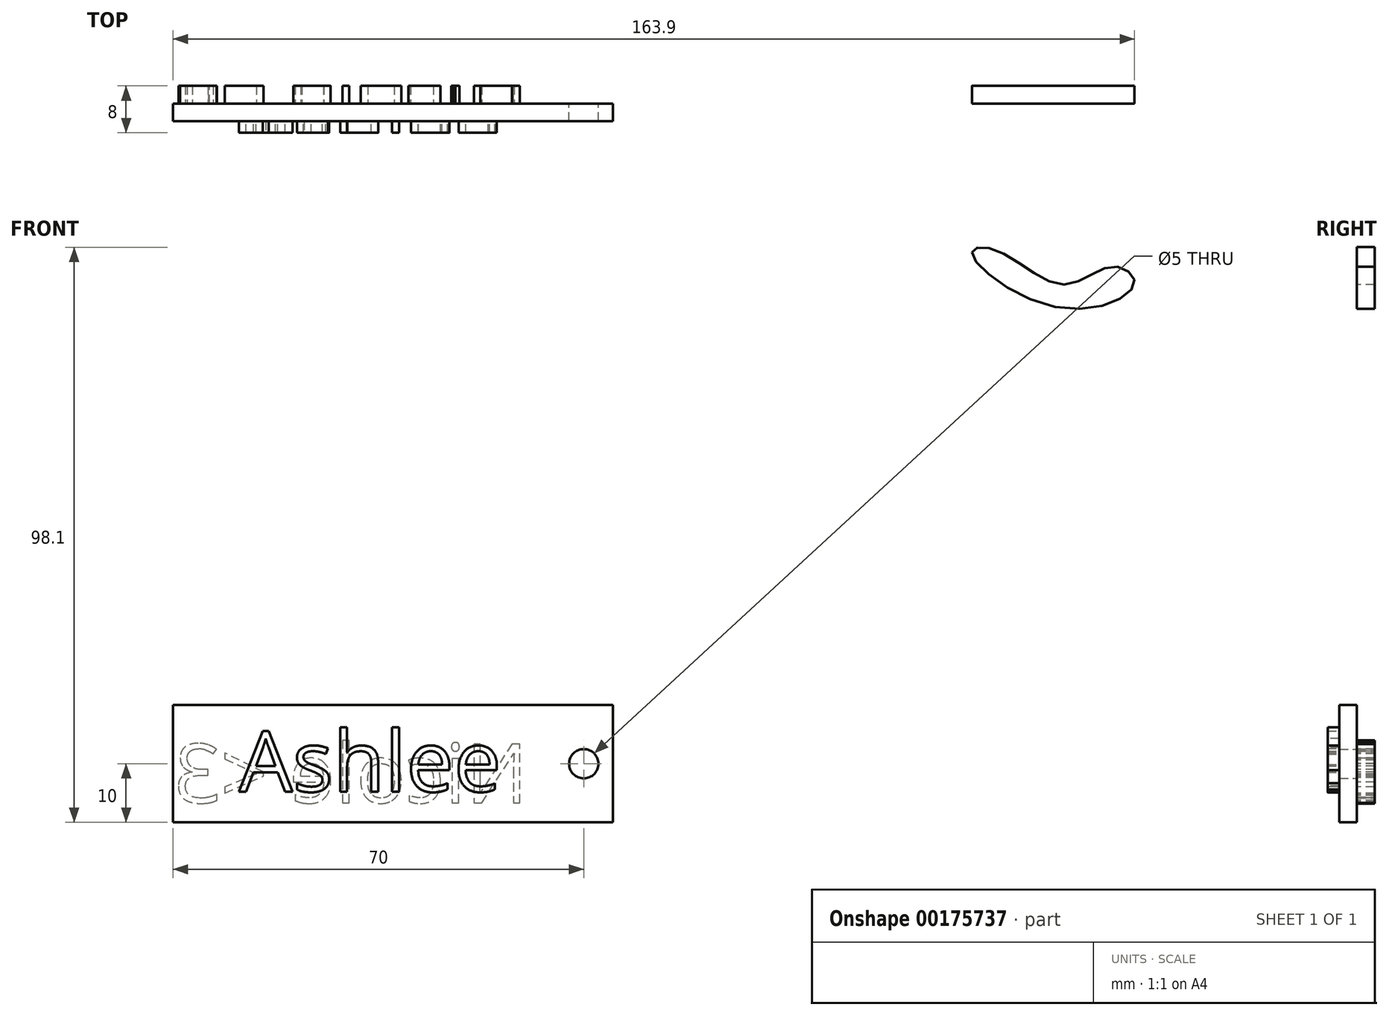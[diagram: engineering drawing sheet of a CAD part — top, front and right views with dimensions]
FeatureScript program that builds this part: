
annotation { "Feature Type Name" : "Feature", "Feature Type Description" : "" }
export const myFeature = defineFeature(function(context is Context, id is Id, definition is map)
    precondition{}
    {
        {
            var Q0;
            Q0=qCreatedBy(makeId("Front.planeOp"),FACE);
            var sketch = newSketch(context, id + "F0", { "sketchPlane" : qUnion([Q0])});
            skLineSegment(sketch, "E0.bottom", {"start": v(0, 0) * mm, "end": v(75, 0) * mm});
            skLineSegment(sketch, "E0.top", {"start": v(0, -20) * mm, "end": v(75, -20) * mm});
            skLineSegment(sketch, "E0.left", {"start": v(0, 0) * mm, "end": v(0, -20) * mm});
            skLineSegment(sketch, "E0.right", {"start": v(75, 0) * mm, "end": v(75, -20) * mm});
            skCircle(sketch, "E1", {"center": v(70, -10) * mm, "radius": 2.5 * mm});
            skSolve(sketch);
        }
        {
            var Q0;
            Q0=makeQuery(id+"F0.imprint","IMPRINT",FACE,{"disambiguationData":[TD([[makeQuery(id+"F0.imprint","IMPRINT",EDGE,{"derivedFrom":sQuery(id+"F0.wireOp",EDGE,"E0.bottom")}),-1.0]])]});
            extrude(context, id + "F1", {"entities" : qUnion([Q0]), "depth" : 3 * mm});
        }
        {
            var Q0;
            Q0=makeQuery(id+"F1.opExtrude","CAP_FACE",FACE,{"disambiguationData":[OSD([sQuery(id+"F0.wireOp",EDGE,"E0.bottom"),sQuery(id+"F0.wireOp",EDGE,"E0.top"),sQuery(id+"F0.wireOp",EDGE,"E0.left"),sQuery(id+"F0.wireOp",EDGE,"E0.right"),sQuery(id+"F0.wireOp",EDGE,"E1")])],"isStart":false});
            var sketch = newSketch(context, id + "F2", { "sketchPlane" : qUnion([Q0])});
            skText(sketch, "E2", { "text": "Ashlee", "fontName": "OpenSans-Regular.ttf"});
            const initialGuessF2  = {"E2": [0.01123, -0.01474, 1, 0, 0.01039]};
            skSetInitialGuess(sketch, initialGuessF2);
            skSolve(sketch);
        }
        {
            var Q0;
            Q0 = qSketchRegion(id + "F2", true);
            extrude(context, id + "F3", {"entities" : qUnion([Q0]), "operationType" : NewBodyOperationType.ADD, "depth" : 2 * mm});
        }
        {
            var Q0;
            Q0=makeQuery(id+"F1.opExtrude","CAP_FACE",FACE,{"disambiguationData":[OSD([sQuery(id+"F0.wireOp",EDGE,"E0.bottom"),sQuery(id+"F0.wireOp",EDGE,"E0.top"),sQuery(id+"F0.wireOp",EDGE,"E0.left"),sQuery(id+"F0.wireOp",EDGE,"E0.right"),sQuery(id+"F0.wireOp",EDGE,"E1")])],"isStart":true});
            var sketch = newSketch(context, id + "F4", { "sketchPlane" : qUnion([Q0])});
            skText(sketch, "E3", { "text": "Nicole <3", "fontName": "OpenSans-Regular.ttf"});
            skFitSpline(sketch, "E4", {"points": [v(-136.18, 77.23) * mm, v(-140.44, 77.53) * mm, v(-151.71, 71.74) * mm, v(-160.24, 74.79) * mm, v(-163.9, 72.05) * mm, v(-151.1, 67.78) * mm, v(-136.18, 77.23) * mm]});
            const initialGuessF4  = {"E3": [-0.06047, -0.01665, 1, 0, 0.0101]};
            skSetInitialGuess(sketch, initialGuessF4);
            skSolve(sketch);
        }
        {
            var Q0;
            Q0 = qSketchRegion(id + "F4", true);
            extrude(context, id + "F5", {"entities" : qUnion([Q0]), "operationType" : NewBodyOperationType.ADD, "depth" : 3 * mm});
        }
    });
